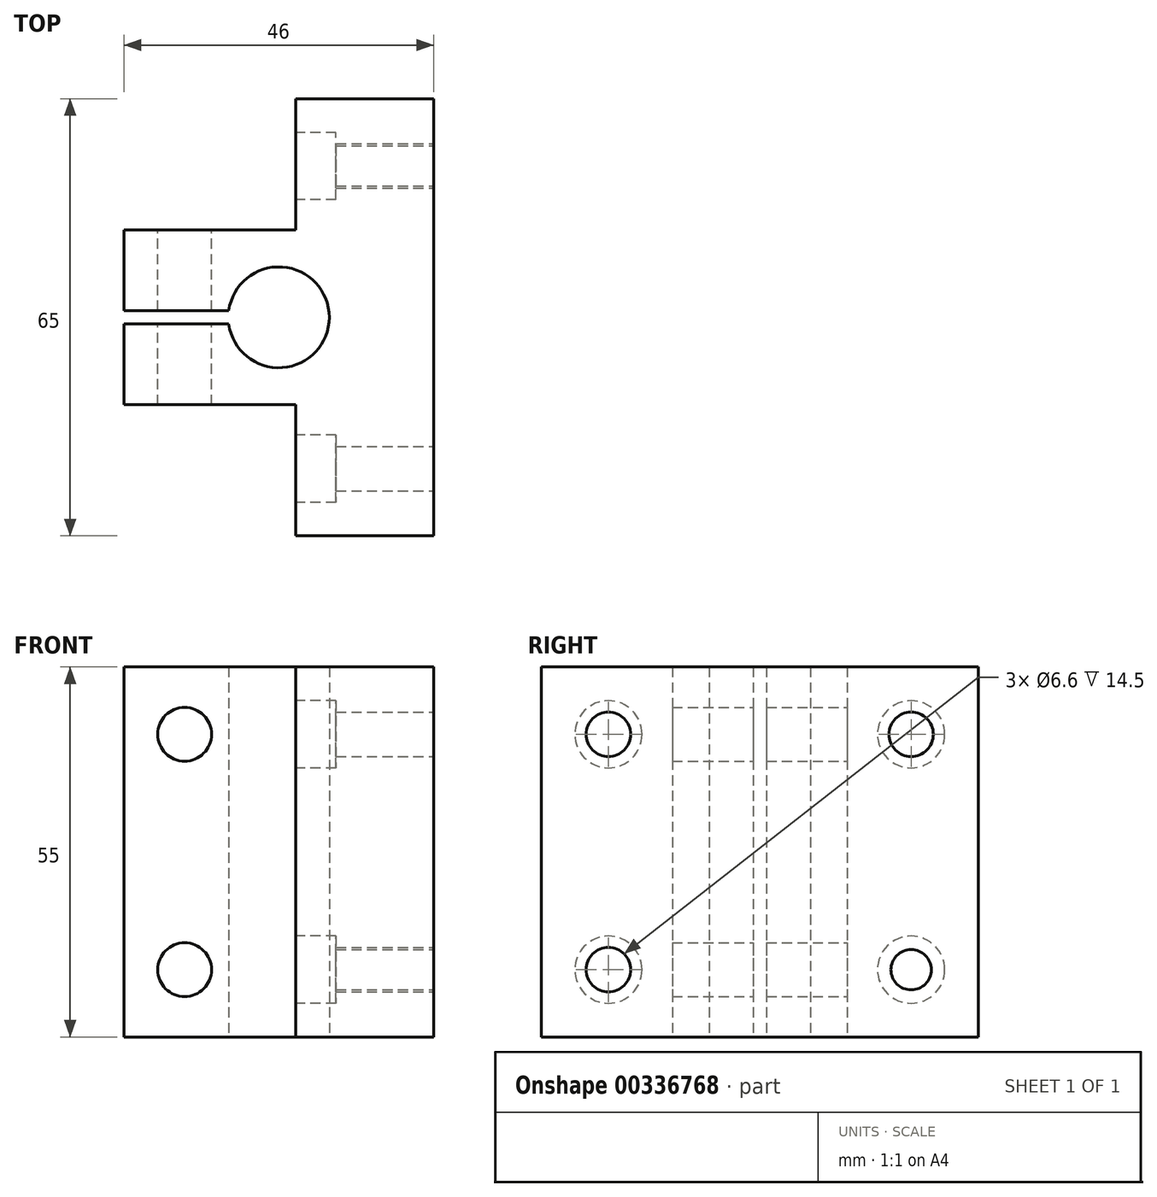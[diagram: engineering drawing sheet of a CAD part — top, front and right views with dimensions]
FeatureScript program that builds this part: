
annotation { "Feature Type Name" : "Feature", "Feature Type Description" : "" }
export const myFeature = defineFeature(function(context is Context, id is Id, definition is map)
    precondition{}
    {
        {
            var Q0;
            Q0=qCreatedBy(makeId("Top.planeOp"),FACE);
            var sketch = newSketch(context, id + "F0", { "sketchPlane" : qUnion([Q0])});
            skLineSegment(sketch, "E0", {"start": v(22.92, 25.64) * mm, "end": v(22.92, 15.64) * mm});
            skLineSegment(sketch, "E1", {"start": v(22.92, 15.64) * mm, "end": v(22.92, -29.36) * mm});
            skLineSegment(sketch, "E2", {"start": v(22.92, -29.36) * mm, "end": v(22.92, -39.36) * mm});
            skLineSegment(sketch, "E3", {"start": v(22.92, 25.64) * mm, "end": v(8.42, 25.64) * mm});
            skLineSegment(sketch, "E4", {"start": v(8.42, 25.64) * mm, "end": v(2.42, 25.64) * mm});
            skLineSegment(sketch, "E5", {"start": v(22.92, -39.36) * mm, "end": v(2.42, -39.36) * mm});
            skLineSegment(sketch, "E6", {"start": v(2.42, -39.36) * mm, "end": v(2.42, -19.86) * mm});
            skLineSegment(sketch, "E7", {"start": v(-23.08, -19.86) * mm, "end": v(-0.08, -19.86) * mm});
            skLineSegment(sketch, "E8", {"start": v(-0.08, -19.86) * mm, "end": v(2.42, -19.86) * mm});
            skLineSegment(sketch, "E9", {"start": v(-23.08, 6.14) * mm, "end": v(2.42, 6.14) * mm});
            skLineSegment(sketch, "E10", {"start": v(2.42, 6.14) * mm, "end": v(2.42, 25.64) * mm});
            skLineSegment(sketch, "E11", {"start": v(-23.08, -19.86) * mm, "end": v(-23.08, -7.86) * mm});
            skLineSegment(sketch, "E12", {"start": v(-23.08, -5.86) * mm, "end": v(-23.08, 6.14) * mm});
            skPoint(sketch, "E13", {"position": v(-0.08, -6.86) * mm});
            skArc(sketch, "E14", {"start": v(-7.51, -7.86) * mm, "mid": v(7.42, -6.86) * mm, "end": v(-7.51, -5.86) * mm});
            skPoint(sketch, "E15.end.orphan", {"position": v(-23.08, -6.86) * mm});
            skLineSegment(sketch, "E16", {"start": v(-23.08, -7.86) * mm, "end": v(-7.51, -7.86) * mm});
            skLineSegment(sketch, "E17", {"start": v(-23.08, -5.86) * mm, "end": v(-7.51, -5.86) * mm});
            skSolve(sketch);
        }
        {
            var Q0;
            Q0 = qSketchRegion(id + "F0", true);
            extrude(context, id + "F1", {"entities" : qUnion([Q0]), "depth" : 55 * mm});
        }
        {
            var Q0;
            Q0=makeQuery(id+"F1.opExtrude","SWEPT_FACE",FACE,{"disambiguationData":[OSD([sQuery(id+"F0.wireOp",EDGE,"E9")])]});
            var sketch = newSketch(context, id + "F2", { "sketchPlane" : qUnion([Q0])});
            skLineSegment(sketch, "E18", {"start": v(23.08, 55) * mm, "end": v(14.08, 55) * mm});
            skLineSegment(sketch, "E19", {"start": v(23.08, 55) * mm, "end": v(23.08, 45) * mm});
            skPoint(sketch, "E20", {"position": v(14.08, 45) * mm});
            skLineSegment(sketch, "E21", {"start": v(23.08, 0) * mm, "end": v(14.08, 0) * mm});
            skLineSegment(sketch, "E22", {"start": v(23.08, 0) * mm, "end": v(23.08, 10) * mm});
            skPoint(sketch, "E23", {"position": v(14.08, 10) * mm});
            skCircle(sketch, "E24", {"center": v(14.08, 10) * mm, "radius": 4 * mm});
            skCircle(sketch, "E25", {"center": v(14.08, 45) * mm, "radius": 4 * mm});
            skSolve(sketch);
        }
        {
            var Q0;
            Q0 = qSketchRegion(id + "F2", true);
            extrude(context, id + "F3", {"entities" : qUnion([Q0]), "operationType" : NewBodyOperationType.REMOVE, "oppositeDirection" : true, "depth" : 60 * mm});
        }
        {
            var Q0;
            Q0=makeQuery(id+"F1.opExtrude","SWEPT_FACE",FACE,{"disambiguationData":[OSD([sQuery(id+"F0.wireOp",EDGE,"E0"),sQuery(id+"F0.wireOp",EDGE,"E1"),sQuery(id+"F0.wireOp",EDGE,"E2")])]});
            var sketch = newSketch(context, id + "F4", { "sketchPlane" : qUnion([Q0])});
            skLineSegment(sketch, "E26", {"start": v(-39.36, 0) * mm, "end": v(-29.36, 0) * mm});
            skLineSegment(sketch, "E27", {"start": v(25.64, 0) * mm, "end": v(15.64, 0) * mm});
            skLineSegment(sketch, "E28", {"start": v(-39.36, 0) * mm, "end": v(-39.36, 10) * mm});
            skPoint(sketch, "E29", {"position": v(-29.36, 10) * mm});
            skPoint(sketch, "E30", {"position": v(15.64, 10) * mm});
            skCircle(sketch, "E31", {"center": v(15.64, 10) * mm, "radius": 3 * mm});
            skCircle(sketch, "E32", {"center": v(-29.36, 10) * mm, "radius": 3.3 * mm});
            skCircle(sketch, "E33", {"center": v(-29.36, 10) * mm, "radius": 5 * mm});
            skCircle(sketch, "E34", {"center": v(15.64, 10) * mm, "radius": 5 * mm});
            skLineSegment(sketch, "E35", {"start": v(-39.36, 55) * mm, "end": v(-39.36, 45) * mm});
            skLineSegment(sketch, "E36", {"start": v(25.64, 55) * mm, "end": v(25.64, 45) * mm});
            skPoint(sketch, "E37", {"position": v(-29.36, 45) * mm});
            skPoint(sketch, "E38", {"position": v(15.64, 45) * mm});
            skCircle(sketch, "E39", {"center": v(-29.36, 45) * mm, "radius": 5 * mm});
            skCircle(sketch, "E40", {"center": v(15.64, 45) * mm, "radius": 5 * mm});
            skCircle(sketch, "E41", {"center": v(15.64, 45) * mm, "radius": 3.3 * mm});
            skCircle(sketch, "E42", {"center": v(-29.36, 45) * mm, "radius": 3.3 * mm});
            skSolve(sketch);
        }
        {
            var Q0;
            Q0=makeQuery(id+"F4.imprint","IMPRINT",FACE,{"disambiguationData":[TD([[makeQuery(id+"F4.imprint","IMPRINT",EDGE,{"derivedFrom":sQuery(id+"F4.wireOp",EDGE,"E32")}),1.0]])]});
            var Q1;
            Q1=makeQuery(id+"F4.imprint","IMPRINT",FACE,{"disambiguationData":[TD([[makeQuery(id+"F4.imprint","IMPRINT",EDGE,{"derivedFrom":sQuery(id+"F4.wireOp",EDGE,"E31")}),1.0]])]});
            var Q2;
            Q2=makeQuery(id+"F4.imprint","IMPRINT",FACE,{"disambiguationData":[TD([[makeQuery(id+"F4.imprint","IMPRINT",EDGE,{"derivedFrom":sQuery(id+"F4.wireOp",EDGE,"E41")}),1.0]])]});
            var Q3;
            Q3=makeQuery(id+"F4.imprint","IMPRINT",FACE,{"disambiguationData":[TD([[makeQuery(id+"F4.imprint","IMPRINT",EDGE,{"derivedFrom":sQuery(id+"F4.wireOp",EDGE,"E42")}),1.0]])]});
            extrude(context, id + "F5", {"entities" : qUnion([Q0, Q1, Q2, Q3]), "operationType" : NewBodyOperationType.REMOVE, "oppositeDirection" : true, "depth" : 14.5 * mm});
        }
        {
            var Q0;
            Q0=makeQuery(id+"F1.opExtrude","SWEPT_FACE",FACE,{"disambiguationData":[OSD([sQuery(id+"F0.wireOp",EDGE,"E6")])]});
            var sketch = newSketch(context, id + "F6", { "sketchPlane" : qUnion([Q0])});
            skLineSegment(sketch, "E43", {"start": v(39.36, 0) * mm, "end": v(29.36, 0) * mm});
            skLineSegment(sketch, "E44", {"start": v(39.36, 0) * mm, "end": v(39.36, 10) * mm});
            skLineSegment(sketch, "E45", {"start": v(39.36, 55) * mm, "end": v(39.36, 45) * mm});
            skPoint(sketch, "E46", {"position": v(29.36, 10) * mm});
            skPoint(sketch, "E47", {"position": v(29.36, 45) * mm});
            skCircle(sketch, "E48", {"center": v(29.36, 45) * mm, "radius": 5 * mm});
            skCircle(sketch, "E49", {"center": v(29.36, 10) * mm, "radius": 5 * mm});
            skSolve(sketch);
        }
        {
            var Q0;
            Q0=makeQuery(id+"F6.imprint","IMPRINT",FACE,{"disambiguationData":[TD([[makeQuery(id+"F6.imprint","IMPRINT",EDGE,{"derivedFrom":sQuery(id+"F6.wireOp",EDGE,"E48")}),1.0]])]});
            var Q1;
            Q1=makeQuery(id+"F6.imprint","IMPRINT",FACE,{"disambiguationData":[TD([[makeQuery(id+"F6.imprint","IMPRINT",EDGE,{"derivedFrom":sQuery(id+"F6.wireOp",EDGE,"E49")}),1.0]])]});
            extrude(context, id + "F7", {"entities" : qUnion([Q0, Q1]), "operationType" : NewBodyOperationType.REMOVE, "oppositeDirection" : true, "depth" : 6 * mm});
        }
        {
            var Q0;
            Q0=makeQuery(id+"F1.opExtrude","SWEPT_FACE",FACE,{"disambiguationData":[OSD([sQuery(id+"F0.wireOp",EDGE,"E10")])]});
            var sketch = newSketch(context, id + "F8", { "sketchPlane" : qUnion([Q0])});
            skLineSegment(sketch, "E50", {"start": v(-25.64, 0) * mm, "end": v(-15.64, 0) * mm});
            skLineSegment(sketch, "E51", {"start": v(-25.64, 0) * mm, "end": v(-25.64, 10) * mm});
            skLineSegment(sketch, "E52", {"start": v(-25.64, 55) * mm, "end": v(-25.64, 45) * mm});
            skPoint(sketch, "E53", {"position": v(-15.64, 10) * mm});
            skPoint(sketch, "E54", {"position": v(-15.64, 45) * mm});
            skCircle(sketch, "E55", {"center": v(-15.64, 45) * mm, "radius": 5 * mm});
            skCircle(sketch, "E56", {"center": v(-15.64, 10) * mm, "radius": 5 * mm});
            skSolve(sketch);
        }
        {
            var Q0;
            Q0 = qSketchRegion(id + "F8", true);
            extrude(context, id + "F9", {"entities" : qUnion([Q0]), "operationType" : NewBodyOperationType.REMOVE, "oppositeDirection" : true, "depth" : 6 * mm});
        }
    });
